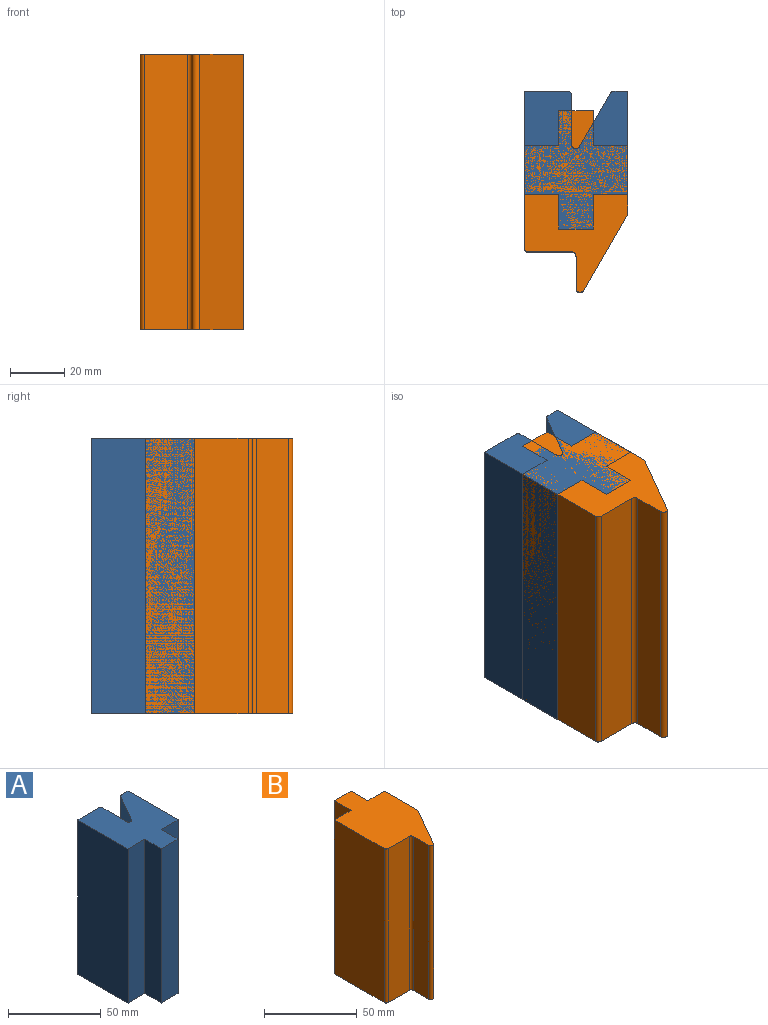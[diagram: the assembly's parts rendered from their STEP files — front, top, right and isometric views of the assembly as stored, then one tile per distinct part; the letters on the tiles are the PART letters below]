
ASSEMBLY  parts=2 mates=2
PART A: 16 faces, bbox 38.1x50.8x101.6 mm
  f0: plane 101.6x12.7mm, normal (1,0,0), area 1290.3mm2, adj f1,f10,f11,f12
  f1: plane 101.6x12.7mm, normal (0,-1,0), area 1290.3mm2, adj f0,f2,f11,f12
  f2: plane 101.6x38.1mm, normal (1,0,0), area 3871mm2, adj f1,f3,f11,f12
  f3: plane 101.6x5.09mm, normal (0,1,0), area 517.4mm2, adj f2,f11,f12,f13
  f4: plane 101.6x19.71mm, normal (-0.87,0.5,0), area 2312.6mm2, adj f11,f12,f13,f14
  f5: plane 101.6x18.19mm, normal (1,0,0), area 1847.9mm2, adj f11,f12,f14,f15
  f6: plane 101.6x15.94mm, normal (0,1,0), area 1619.4mm2, adj f7,f11,f12,f15
  f7: plane 101.6x38.1mm, normal (-1,0,0), area 3871mm2, adj f6,f8,f11,f12
  f8: plane 101.6x12.7mm, normal (0,-1,0), area 1290.3mm2, adj f7,f9,f11,f12
  f9: plane 101.6x12.7mm, normal (-1,0,0), area 1290.3mm2, adj f8,f10,f11,f12
  f10: plane 101.6x12.7mm, normal (0,-1,0), area 1290.3mm2, adj f0,f9,f11,f12
  f11: plane 50.8x38.1mm, normal (0,0,-1), area 1431.7mm2, adj f0,f1,f2,f3,f4,f5,f6,f7
  f12: plane 50.8x38.1mm, normal (0,0,1), area 1431.7mm2, adj f0,f1,f2,f3,f4,f5,f6,f7
  f13: cylinder r=1.52mm len=101.6mm, axis (0,0,-1), area 162.1mm2, adj f3,f4,f11,f12
  f14: cylinder r=1.52mm len=101.6mm, axis (0,0,1), area 405.4mm2, adj f4,f5,f11,f12
  f15: cylinder r=1.52mm len=101.6mm, axis (0,0,-1), area 243.2mm2, adj f5,f6,f11,f12
PART B: 15 faces, bbox 38.1x66.9x101.6 mm
  f0: plane 101.6x12.7mm, normal (0,1,0), area 1290.3mm2, adj f1,f9,f10,f11
  f1: plane 101.6x12.7mm, normal (-1,0,0), area 1290.3mm2, adj f0,f2,f10,f11
  f2: plane 101.6x12.7mm, normal (0,1,0), area 1290.3mm2, adj f1,f3,f10,f11
  f3: plane 101.6x37.82mm, normal (-1,0,0), area 3842.7mm2, adj f2,f10,f11,f12
  f4: plane 101.6x16mm, normal (0,-1,0), area 1625.8mm2, adj f10,f11,f12,f13
  f5: plane 101.6x11.84mm, normal (-1,0,0), area 1202.8mm2, adj f10,f11,f13,f14
  f6: plane 101.6x28.07mm, normal (0.87,-0.5,0), area 3293.1mm2, adj f7,f10,f11,f14
  f7: plane 101.6x25.4mm, normal (1,0,0), area 2580.6mm2, adj f6,f8,f10,f11
  f8: plane 101.6x12.7mm, normal (0,1,0), area 1290.3mm2, adj f7,f9,f10,f11
  f9: plane 101.6x12.7mm, normal (1,0,0), area 1290.3mm2, adj f0,f8,f10,f11
  f10: plane 66.93x38.1mm, normal (0,0,1), area 1703.3mm2, adj f0,f1,f2,f3,f4,f5,f6,f7
  f11: plane 66.93x38.1mm, normal (0,0,-1), area 1703.3mm2, adj f0,f1,f2,f3,f4,f5,f6,f7
  f12: cylinder r=1.52mm len=101.6mm, axis (0,0,-1), area 243.2mm2, adj f3,f4,f10,f11
  f13: cylinder r=1.52mm len=101.6mm, axis (0,0,1), area 243.2mm2, adj f4,f5,f10,f11
  f14: cylinder r=1.52mm len=101.6mm, axis (0,0,-1), area 405.4mm2, adj f5,f6,f10,f11
PLACE A t=(-30.81,-43.18,3.52)mm
PLACE B t=(-37.16,-50.38,3.52)mm
MATE planar B.f10 <-> A.f12  axis (0,0,1) through (-31.12,-81.28,105.12)mm
MATE planar A.f9 <-> B.f1  axis (-1,0,0) through (-37.16,-87.63,54.32)mm
